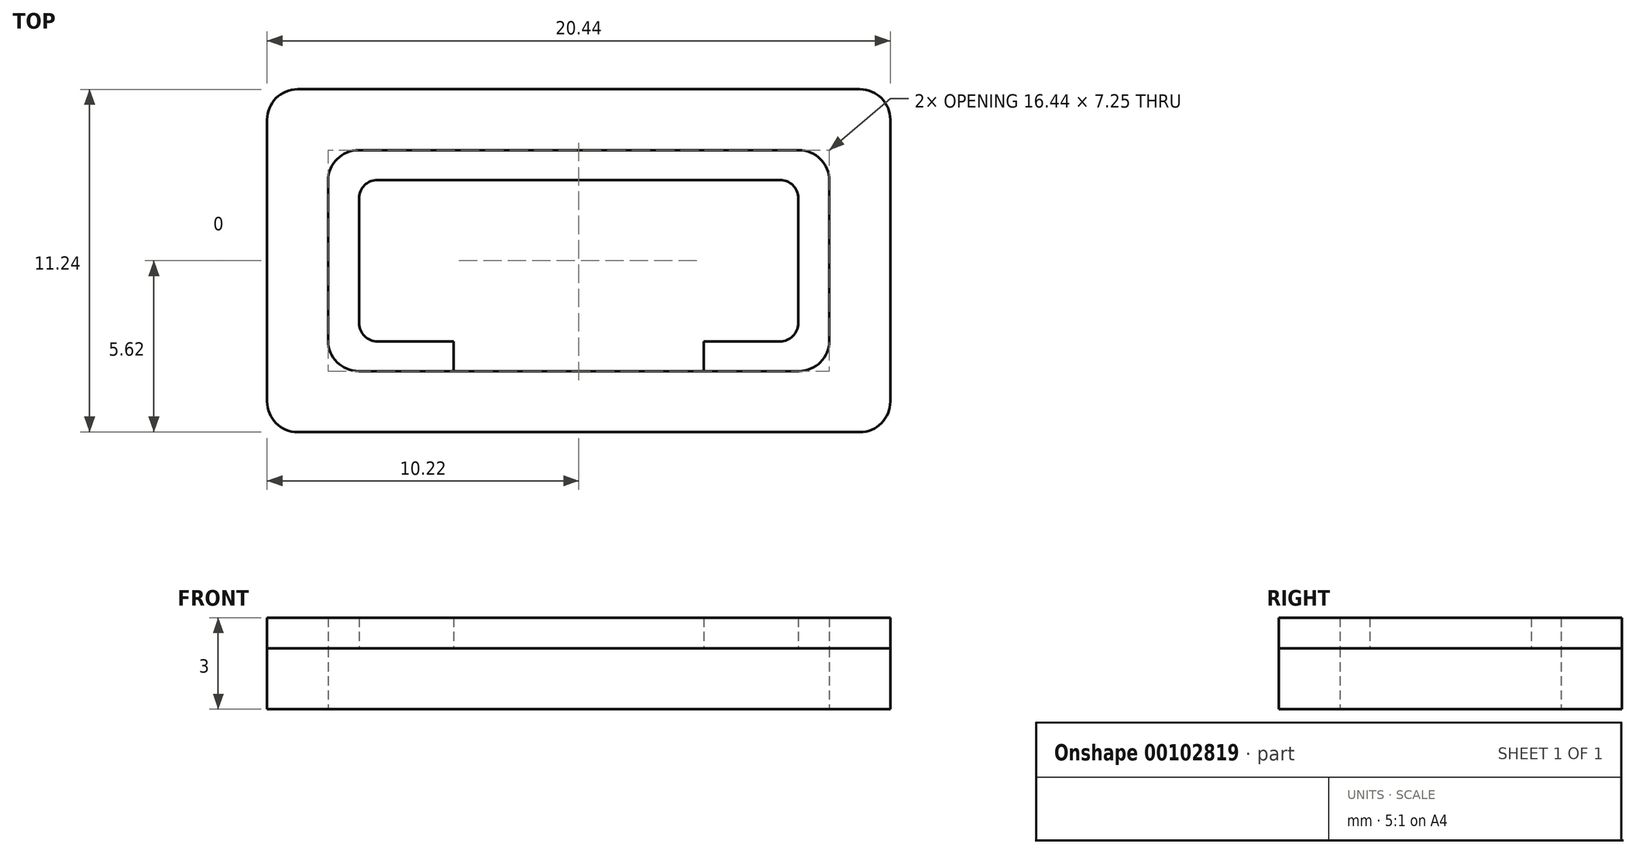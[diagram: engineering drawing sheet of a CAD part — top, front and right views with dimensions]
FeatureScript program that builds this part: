
annotation { "Feature Type Name" : "Feature", "Feature Type Description" : "" }
export const myFeature = defineFeature(function(context is Context, id is Id, definition is map)
    precondition{}
    {
        {
            var Q0;
            Q0=qCreatedBy(makeId("Top.planeOp"),FACE);
            var sketch = newSketch(context, id + "F0", { "sketchPlane" : qUnion([Q0])});
            skLineSegment(sketch, "E0.bottom", {"start": v(8.12, -3.52) * mm, "end": v(-8.12, -3.53) * mm, "construction": true});
            skLineSegment(sketch, "E0.top", {"start": v(8.12, 3.53) * mm, "end": v(-8.12, 3.52) * mm, "construction": true});
            skLineSegment(sketch, "E0.left", {"start": v(8.12, -3.52) * mm, "end": v(8.12, 3.53) * mm, "construction": true});
            skLineSegment(sketch, "E0.right", {"start": v(-8.12, -3.53) * mm, "end": v(-8.12, 3.52) * mm, "construction": true});
            skPoint(sketch, "E0.middle", {"position": v(0, 0) * mm});
            skLineSegment(sketch, "E1.0", {"start": v(7.22, 3.63) * mm, "end": v(-7.22, 3.62) * mm});
            skLineSegment(sketch, "E1.1", {"start": v(8.22, -2.62) * mm, "end": v(8.22, 2.63) * mm});
            skLineSegment(sketch, "E1.2", {"start": v(7.22, -3.62) * mm, "end": v(-7.22, -3.63) * mm});
            skLineSegment(sketch, "E1.3", {"start": v(-8.22, -2.63) * mm, "end": v(-8.22, 2.62) * mm});
            skLineSegment(sketch, "E2.0", {"start": v(9.22, 5.63) * mm, "end": v(-9.22, 5.62) * mm});
            skLineSegment(sketch, "E2.1", {"start": v(10.22, -4.63) * mm, "end": v(10.22, 4.63) * mm});
            skLineSegment(sketch, "E2.2", {"start": v(9.22, -5.62) * mm, "end": v(-9.22, -5.63) * mm});
            skLineSegment(sketch, "E2.3", {"start": v(-10.22, -4.63) * mm, "end": v(-10.22, 4.62) * mm});
            skPoint(sketch, "E3.visualSharp", {"position": v(-8.22, 3.62) * mm});
            skArc(sketch, "E3.filletArc", {"start": v(-7.22, 3.62) * mm, "mid": v(-7.93, 3.33) * mm, "end": v(-8.22, 2.62) * mm});
            skPoint(sketch, "E4.visualSharp", {"position": v(8.22, 3.63) * mm});
            skArc(sketch, "E4.filletArc", {"start": v(8.22, 2.63) * mm, "mid": v(7.93, 3.33) * mm, "end": v(7.22, 3.63) * mm});
            skPoint(sketch, "E5.visualSharp", {"position": v(8.22, -3.62) * mm});
            skArc(sketch, "E5.filletArc", {"start": v(7.22, -3.62) * mm, "mid": v(7.93, -3.33) * mm, "end": v(8.22, -2.62) * mm});
            skPoint(sketch, "E6.visualSharp", {"position": v(-8.22, -3.63) * mm});
            skArc(sketch, "E6.filletArc", {"start": v(-8.22, -2.63) * mm, "mid": v(-7.93, -3.33) * mm, "end": v(-7.22, -3.63) * mm});
            skPoint(sketch, "E7.visualSharp", {"position": v(-10.22, -5.63) * mm});
            skArc(sketch, "E7.filletArc", {"start": v(-10.22, -4.63) * mm, "mid": v(-9.93, -5.33) * mm, "end": v(-9.22, -5.63) * mm});
            skPoint(sketch, "E8.visualSharp", {"position": v(-10.22, 5.62) * mm});
            skArc(sketch, "E8.filletArc", {"start": v(-9.22, 5.62) * mm, "mid": v(-9.93, 5.33) * mm, "end": v(-10.22, 4.62) * mm});
            skPoint(sketch, "E9.visualSharp", {"position": v(10.22, 5.63) * mm});
            skArc(sketch, "E9.filletArc", {"start": v(10.22, 4.63) * mm, "mid": v(9.93, 5.33) * mm, "end": v(9.22, 5.63) * mm});
            skPoint(sketch, "E10.visualSharp", {"position": v(10.22, -5.62) * mm});
            skArc(sketch, "E10.filletArc", {"start": v(9.22, -5.62) * mm, "mid": v(9.93, -5.33) * mm, "end": v(10.22, -4.63) * mm});
            skSolve(sketch);
        }
        {
            var Q0;
            Q0=makeQuery(id+"F0.imprint","IMPRINT",FACE,{"disambiguationData":[TD([[makeQuery(id+"F0.imprint","IMPRINT",EDGE,{"derivedFrom":sQuery(id+"F0.wireOp",EDGE,"E1.0")}),-1.0]])]});
            extrude(context, id + "F1", {"entities" : qUnion([Q0]), "depth" : 2 * mm});
        }
        {
            var Q0;
            Q0=makeQuery(id+"F1.opExtrude","CAP_FACE",FACE,{"disambiguationData":[OSD([sQuery(id+"F0.wireOp",EDGE,"E1.0"),sQuery(id+"F0.wireOp",EDGE,"E1.1"),sQuery(id+"F0.wireOp",EDGE,"E1.2"),sQuery(id+"F0.wireOp",EDGE,"E1.3"),sQuery(id+"F0.wireOp",EDGE,"E2.0"),sQuery(id+"F0.wireOp",EDGE,"E2.1"),sQuery(id+"F0.wireOp",EDGE,"E2.2"),sQuery(id+"F0.wireOp",EDGE,"E2.3"),sQuery(id+"F0.wireOp",EDGE,"E3.filletArc"),sQuery(id+"F0.wireOp",EDGE,"E4.filletArc"),sQuery(id+"F0.wireOp",EDGE,"E5.filletArc"),sQuery(id+"F0.wireOp",EDGE,"E6.filletArc"),sQuery(id+"F0.wireOp",EDGE,"E7.filletArc"),sQuery(id+"F0.wireOp",EDGE,"E8.filletArc"),sQuery(id+"F0.wireOp",EDGE,"E9.filletArc"),sQuery(id+"F0.wireOp",EDGE,"E10.filletArc")])],"isStart":false});
            var sketch = newSketch(context, id + "F2", { "sketchPlane" : qUnion([Q0])});
            skArc(sketch, "E11", {"start": v(10.22, 4.63) * mm, "mid": v(9.93, 5.33) * mm, "end": v(9.22, 5.63) * mm});
            skLineSegment(sketch, "E12", {"start": v(10.22, -4.63) * mm, "end": v(10.22, 4.63) * mm});
            skArc(sketch, "E13", {"start": v(9.22, -5.62) * mm, "mid": v(9.93, -5.33) * mm, "end": v(10.22, -4.63) * mm});
            skLineSegment(sketch, "E14", {"start": v(9.22, -5.62) * mm, "end": v(-9.22, -5.63) * mm});
            skArc(sketch, "E15", {"start": v(-10.22, -4.63) * mm, "mid": v(-9.93, -5.33) * mm, "end": v(-9.22, -5.63) * mm});
            skLineSegment(sketch, "E16", {"start": v(-10.22, -4.63) * mm, "end": v(-10.22, 4.62) * mm});
            skArc(sketch, "E17", {"start": v(-9.22, 5.62) * mm, "mid": v(-9.93, 5.33) * mm, "end": v(-10.22, 4.62) * mm});
            skLineSegment(sketch, "E18", {"start": v(9.22, 5.63) * mm, "end": v(-9.22, 5.62) * mm});
            skArc(sketch, "E19", {"start": v(-7.22, 3.62) * mm, "mid": v(-7.93, 3.33) * mm, "end": v(-8.22, 2.62) * mm});
            skLineSegment(sketch, "E20", {"start": v(-8.22, -2.63) * mm, "end": v(-8.22, 2.62) * mm});
            skArc(sketch, "E21", {"start": v(-8.22, -2.63) * mm, "mid": v(-7.93, -3.33) * mm, "end": v(-7.22, -3.63) * mm});
            skLineSegment(sketch, "E22", {"start": v(7.22, -3.62) * mm, "end": v(-7.22, -3.63) * mm});
            skArc(sketch, "E23", {"start": v(7.22, -3.62) * mm, "mid": v(7.93, -3.33) * mm, "end": v(8.22, -2.62) * mm});
            skLineSegment(sketch, "E24", {"start": v(8.22, -2.62) * mm, "end": v(8.22, 2.63) * mm});
            skArc(sketch, "E25", {"start": v(8.22, 2.63) * mm, "mid": v(7.93, 3.33) * mm, "end": v(7.22, 3.63) * mm});
            skLineSegment(sketch, "E26", {"start": v(7.22, 3.63) * mm, "end": v(-7.22, 3.62) * mm});
            skPoint(sketch, "E27.middle", {"position": v(-0.16, 0) * mm});
            skPoint(sketch, "E27.top.end.orphan", {"position": v(-7.26, 1.64) * mm});
            skPoint(sketch, "E27.bottom.end.orphan", {"position": v(-7.26, -1.64) * mm});
            skPoint(sketch, "E27.left.end.orphan", {"position": v(6.94, 1.64) * mm});
            skPoint(sketch, "E27.left.start.orphan", {"position": v(6.94, -1.64) * mm});
            skLineSegment(sketch, "E28.bottom", {"start": v(6.6, -2.65) * mm, "end": v(-6.6, -2.65) * mm});
            skLineSegment(sketch, "E28.top", {"start": v(6.6, 2.65) * mm, "end": v(-6.6, 2.65) * mm});
            skLineSegment(sketch, "E28.left", {"start": v(7.2, -2.05) * mm, "end": v(7.2, 2.05) * mm});
            skLineSegment(sketch, "E28.right", {"start": v(-7.2, -2.05) * mm, "end": v(-7.2, 2.05) * mm});
            skPoint(sketch, "E28.middle", {"position": v(0, 0) * mm});
            skPoint(sketch, "E29", {"position": v(0, -2.65) * mm});
            skPoint(sketch, "E30", {"position": v(-4.1, -2.65) * mm});
            skPoint(sketch, "E31", {"position": v(4.1, -2.65) * mm});
            skLineSegment(sketch, "E32", {"start": v(-4.1, -2.65) * mm, "end": v(-4.1, -3.63) * mm});
            skLineSegment(sketch, "E33", {"start": v(4.1, -2.65) * mm, "end": v(4.1, -3.62) * mm});
            skPoint(sketch, "E34.visualSharp", {"position": v(-7.2, 2.65) * mm});
            skArc(sketch, "E34.filletArc", {"start": v(-6.6, 2.65) * mm, "mid": v(-7.02, 2.47) * mm, "end": v(-7.2, 2.05) * mm});
            skPoint(sketch, "E35.visualSharp", {"position": v(7.2, 2.65) * mm});
            skArc(sketch, "E35.filletArc", {"start": v(7.2, 2.05) * mm, "mid": v(7.02, 2.47) * mm, "end": v(6.6, 2.65) * mm});
            skPoint(sketch, "E36.visualSharp", {"position": v(7.2, -2.65) * mm});
            skArc(sketch, "E36.filletArc", {"start": v(6.6, -2.65) * mm, "mid": v(7.02, -2.47) * mm, "end": v(7.2, -2.05) * mm});
            skPoint(sketch, "E37.visualSharp", {"position": v(-7.2, -2.65) * mm});
            skArc(sketch, "E37.filletArc", {"start": v(-7.2, -2.05) * mm, "mid": v(-7.02, -2.47) * mm, "end": v(-6.6, -2.65) * mm});
            skSolve(sketch);
        }
        {
            var Q0;
            Q0=makeQuery(id+"F2.imprint","IMPRINT",FACE,{"disambiguationData":[TD([[makeQuery(id+"F2.imprint","IMPRINT",EDGE,{"derivedFrom":sQuery(id+"F2.wireOp",EDGE,"E19")}),1.0]])]});
            extrude(context, id + "F3", {"entities" : qUnion([Q0]), "depth" : 1 * mm});
        }
        {
            var Q0;
            Q0=makeQuery(id+"F1.opExtrude","CAP_FACE",FACE,{"disambiguationData":[OSD([sQuery(id+"F0.wireOp",EDGE,"E1.0"),sQuery(id+"F0.wireOp",EDGE,"E1.1"),sQuery(id+"F0.wireOp",EDGE,"E1.2"),sQuery(id+"F0.wireOp",EDGE,"E1.3"),sQuery(id+"F0.wireOp",EDGE,"E2.0"),sQuery(id+"F0.wireOp",EDGE,"E2.1"),sQuery(id+"F0.wireOp",EDGE,"E2.2"),sQuery(id+"F0.wireOp",EDGE,"E2.3"),sQuery(id+"F0.wireOp",EDGE,"E3.filletArc"),sQuery(id+"F0.wireOp",EDGE,"E4.filletArc"),sQuery(id+"F0.wireOp",EDGE,"E5.filletArc"),sQuery(id+"F0.wireOp",EDGE,"E6.filletArc"),sQuery(id+"F0.wireOp",EDGE,"E7.filletArc"),sQuery(id+"F0.wireOp",EDGE,"E8.filletArc"),sQuery(id+"F0.wireOp",EDGE,"E9.filletArc"),sQuery(id+"F0.wireOp",EDGE,"E10.filletArc")])],"isStart":false});
            extrude(context, id + "F4", {"entities" : qUnion([Q0]), "depth" : 1 * mm});
        }
    });
